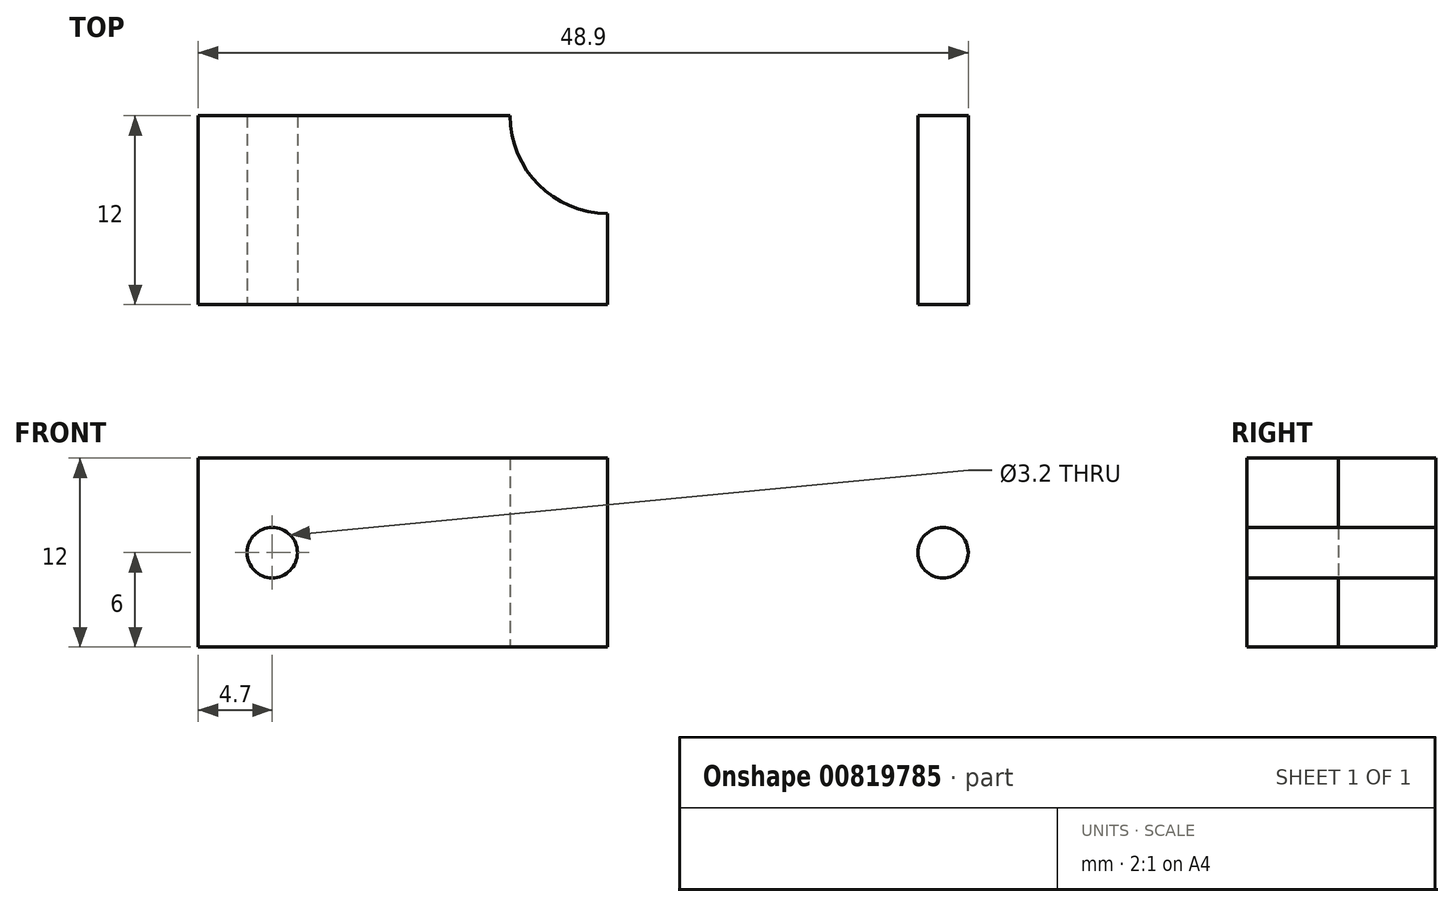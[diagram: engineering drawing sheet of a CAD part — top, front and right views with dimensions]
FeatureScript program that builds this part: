
annotation { "Feature Type Name" : "Feature", "Feature Type Description" : "" }
export const myFeature = defineFeature(function(context is Context, id is Id, definition is map)
    precondition{}
    {
        {
            var Q0;
            Q0=qCreatedBy(makeId("Top.planeOp"),FACE);
            var sketch = newSketch(context, id + "F0", { "sketchPlane" : qUnion([Q0])});
            skLineSegment(sketch, "E0", {"start": v(0, 0) * mm, "end": v(0, -12) * mm});
            skSolve(sketch);
        }
        {
            var Q0;
            Q0=qCreatedBy(makeId("Top.planeOp"),FACE);
            var sketch = newSketch(context, id + "F1", { "sketchPlane" : qUnion([Q0])});
            skLineSegment(sketch, "E1.bottom", {"start": v(6.2, 0) * mm, "end": v(26, 0) * mm});
            skLineSegment(sketch, "E1.top", {"start": v(0, -12) * mm, "end": v(26, -12) * mm});
            skLineSegment(sketch, "E1.left", {"start": v(0, -6.2) * mm, "end": v(0, -12) * mm});
            skLineSegment(sketch, "E1.right", {"start": v(26, 0) * mm, "end": v(26, -12) * mm});
            skArc(sketch, "E2", {"start": v(0, -8) * mm, "mid": v(5.66, -5.66) * mm, "end": v(8, 0) * mm});
            skArc(sketch, "E3", {"start": v(0, -6.2) * mm, "mid": v(4.38, -4.38) * mm, "end": v(6.2, 0) * mm});
            skArc(sketch, "E4.MirrorCS", {"start": v(0, -6.2) * mm, "mid": v(-4.38, -4.38) * mm, "end": v(-6.2, 0) * mm});
            skLineSegment(sketch, "E5.MirrorCS", {"start": v(-6.2, 0) * mm, "end": v(-26, 0) * mm});
            skArc(sketch, "E6.MirrorCS", {"start": v(0, -8) * mm, "mid": v(-5.66, -5.66) * mm, "end": v(-8, 0) * mm});
            skLineSegment(sketch, "E7.MirrorCS", {"start": v(-26, 0) * mm, "end": v(-26, -12) * mm});
            skLineSegment(sketch, "E8.MirrorCS", {"start": v(0, -12) * mm, "end": v(-26, -12) * mm});
            skSolve(sketch);
        }
        {
            var Q0;
            Q0 = qSketchRegion(id + "F1", true);
            extrude(context, id + "F2", {"entities" : qUnion([Q0]), "depth" : 12 * mm, "offsetDistance" : 25 * mm});
        }
        {
            var Q0;
            {var subQ0=sQuery(id+"F1.wireOp",EDGE,"E4.MirrorCS");Q0=makeQuery(id+"F1.imprint","IMPRINT",FACE,{"disambiguationData":[TD([[makeQuery(id+"F1.imprint","IMPRINT",EDGE,{"derivedFrom":subQ0}),1.0]])]});}
            var Q1;
            {var subQ2=sQuery(id+"F1.wireOp",EDGE,"E2");Q1=makeQuery(id+"F1.imprint","IMPRINT",FACE,{"disambiguationData":[TD([[makeQuery(id+"F1.imprint","IMPRINT",EDGE,{"derivedFrom":subQ2}),1.0]])]});}
            extrude(context, id + "F3", {"entities" : qUnion([Q0, Q1]), "operationType" : NewBodyOperationType.REMOVE, "depth" : 6 * mm, "offsetDistance" : 25 * mm});
        }
        {
            var Q0;
            Q0=makeQuery(id+"F2.opExtrude","SWEPT_FACE",FACE,{"disambiguationData":[OSD([sQuery(id+"F1.wireOp",EDGE,"E1.top"),sQuery(id+"F1.wireOp",EDGE,"E8.MirrorCS")])]});
            var sketch = newSketch(context, id + "F4", { "sketchPlane" : qUnion([Q0])});
            skLineSegment(sketch, "E9", {"start": v(-26, 6) * mm, "end": v(26, 6) * mm, "construction": true});
            skLineSegment(sketch, "E10", {"start": v(0, 12) * mm, "end": v(0, 0) * mm});
            skCircle(sketch, "E11", {"center": v(-21.3, 6) * mm, "radius": 1.6 * mm});
            skCircle(sketch, "E12.MirrorC", {"center": v(21.3, 6) * mm, "radius": 1.6 * mm});
            skSolve(sketch);
        }
        {
            var Q0;
            Q0=makeQuery(id+"F4.imprint","IMPRINT",FACE,{"disambiguationData":[TD([[makeQuery(id+"F4.imprint","IMPRINT",EDGE,{"derivedFrom":sQuery(id+"F4.wireOp",EDGE,"E11")}),1.0]])]});
            var Q1;
            Q1=makeQuery(id+"F4.imprint","IMPRINT",FACE,{"disambiguationData":[TD([[makeQuery(id+"F4.imprint","IMPRINT",EDGE,{"derivedFrom":sQuery(id+"F4.wireOp",EDGE,"E12.MirrorC")}),-1.0]])]});
            extrude(context, id + "F5", {"entities" : qUnion([Q0, Q1]), "operationType" : NewBodyOperationType.REMOVE, "oppositeDirection" : true, "depth" : 25 * mm, "offsetDistance" : 25 * mm});
        }
    });
